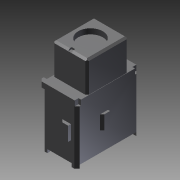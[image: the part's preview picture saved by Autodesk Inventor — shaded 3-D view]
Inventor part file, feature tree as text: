
AUTODESK INVENTOR PART (.ipt)
format: ipt  version: 2011 SP1 (Build 150282100, 282)  size: 208,384 bytes
history: native  units: in
note: dims shown in document units (in); Inventor stores cm internally (conversion verified against a paired STEP export)
features: other x56, sketch x13, extrude x12, hole x1
ambient origin geometry x8: Origin, YZ Plane, XZ Plane, XY Plane, X Axis, Y Axis, Z Axis, Center Point
bodies: Solid1 (feature_tree)
feature tree (82):
  extrude  "Extrusion1"  Depth=0.02in TaperAngle=0.0deg
  extrude  "Extrusion2"  Depth=0.03in TaperAngle=0.0deg
  extrude  "Extrusion3"  Depth=0.08in TaperAngle=0.0deg
  extrude  "Extrusion4"  Depth=0.08in TaperAngle=0.0deg
  extrude  "Extrusion5"  Depth=0.197in TaperAngle=0.0deg
  extrude  "Extrusion6"  Depth=0.01in TaperAngle=0.0deg
  extrude  "Extrusion7"  [1 undecoded]
  extrude  "Extrusion8"  [1 undecoded]
  extrude  "Extrusion9"  [1 undecoded]
  extrude  "Extrusion10"  [1 undecoded]
  extrude  "Extrusion11"  [1 undecoded]
  hole  "Drilling 1"  [1 undecoded]
  extrude  "Extrusion12"  [1 undecoded]
  other  "to_bracket_r_XY"
  other  "to_bracket_r_YZ"
  other  "to_bracket_r_ZX"
  other  "to_bracket_r_X"
  other  "to_bracket_r_Y"
  other  "to_bracket_r_Z"
  other  "to_bracket_r_Center"
  other  "to_bracket_r2_XY"
  other  "to_bracket_r2_YZ"
  other  "to_bracket_r2_ZX"
  other  "to_bracket_r2_X"
  other  "to_bracket_r2_Y"
  other  "to_bracket_r2_Z"
  other  "to_bracket_r2_Center"
  other  "to_bracket_s_XY"
  other  "to_bracket_s_YZ"
  other  "to_bracket_s_ZX"
  other  "to_bracket_s_X"
  other  "to_bracket_s_Y"
  other  "to_bracket_s_Z"
  other  "to_bracket_s_Center"
  other  "to_bracket_s2_XY"
  other  "to_bracket_s2_YZ"
  other  "to_bracket_s2_ZX"
  other  "to_bracket_s2_X"
  other  "to_bracket_s2_Y"
  other  "to_bracket_s2_Z"
  other  "to_bracket_s2_Center"
  other  "to_bracket_v_XY"
  other  "to_bracket_v_YZ"
  other  "to_bracket_v_ZX"
  other  "to_bracket_v_X"
  other  "to_bracket_v_Y"
  other  "to_bracket_v_Z"
  other  "to_bracket_v_Center"
  other  "to_dummy_XY"
  other  "to_dummy_YZ"
  other  "to_dummy_ZX"
  other  "to_dummy_X"
  other  "to_dummy_Y"
  other  "to_dummy_Z"
  other  "to_dummy_Center"
  other  "to_terminal_XY"
  other  "to_terminal_YZ"
  other  "to_terminal_ZX"
  other  "to_terminal_X"
  other  "to_terminal_Y"
  other  "to_terminal_Z"
  other  "to_terminal_Center"
  other  "to_toggle_XY"
  other  "to_toggle_YZ"
  other  "to_toggle_ZX"
  other  "to_toggle_X"
  other  "to_toggle_Y"
  other  "to_toggle_Z"
  other  "to_toggle_Center"
  sketch  "Sketch_1"  dims[d0=0.339in d1=0.0in d2=0.02in d3=0.0in]
  sketch  "Sketch_2"  dims[d4=0.036in d5=0.0in d6=0.03in d7=0.0in]
  sketch  "Sketch_21"
  sketch  "Sketch_3"  dims[d8=0.03in d9=0.0in d10=0.08in d11=0.0in]
  sketch  "Sketch_4"  dims[d12=0.08in d13=0.0in d14=0.08in d15=0.0in]
  sketch  "Sketch_5"  dims[d16=0.177in d17=0.0in d18=0.197in d19=0.0in]
  sketch  "Sketch_6"  dims[d20=0.236in d21=0.0in]
  sketch  "Sketch_7"  dims[d22=0.14in d23=0.75in d24=0.375in d25=0.25in d26=0.5635in d27=0.03in d28=0.0in d29=0.01in d30=0.0in]
  sketch  "Sketch_8"
  sketch  "Sketch_9"
  sketch  "Sketch_10"
  sketch  "Sketch12"
  sketch  "Sketch_28"
note: 7 required parameter values undecoded (feature->parameter linkage not recoverable at this tier; creation-order binding heuristic only, values carry confidence <= 0.55)
